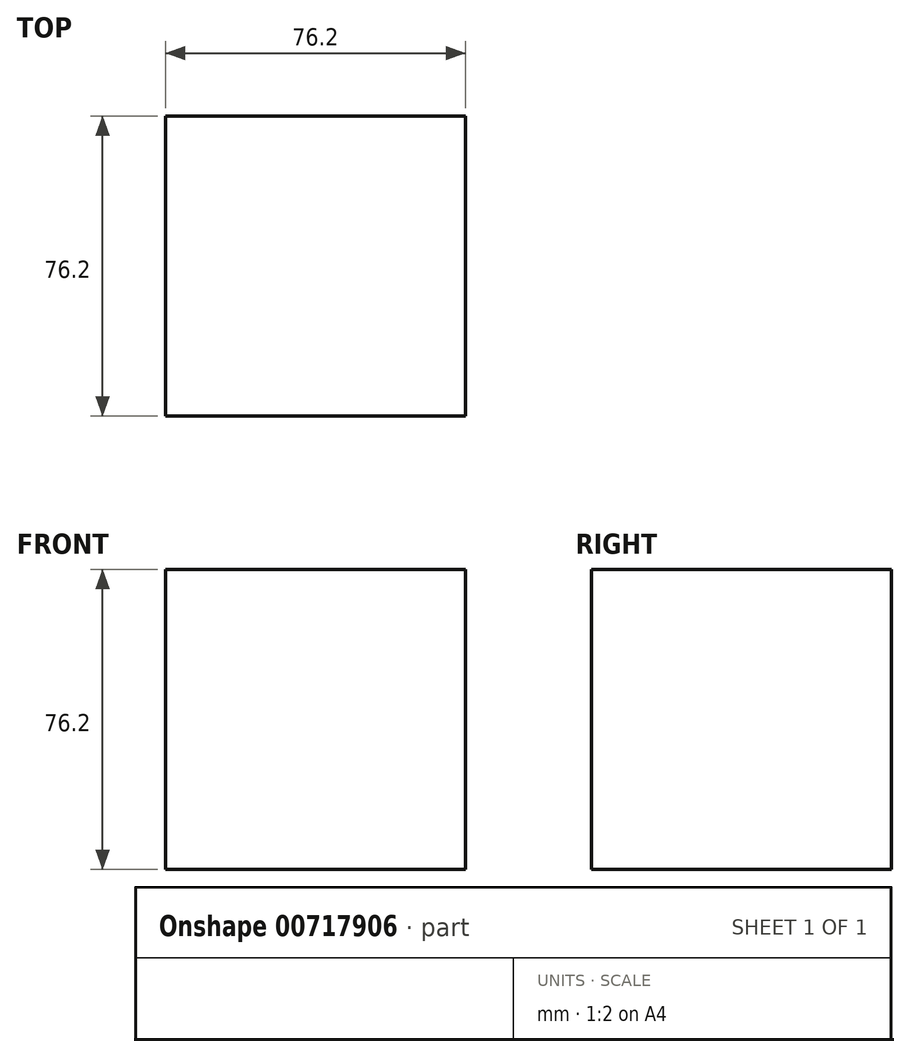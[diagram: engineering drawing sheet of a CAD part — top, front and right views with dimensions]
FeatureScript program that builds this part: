
annotation { "Feature Type Name" : "Feature", "Feature Type Description" : "" }
export const myFeature = defineFeature(function(context is Context, id is Id, definition is map)
    precondition{}
    {
        {
            var Q0;
            Q0=qCreatedBy(makeId("Front.planeOp"),FACE);
            var sketch = newSketch(context, id + "F0", { "sketchPlane" : qUnion([Q0])});
            skLineSegment(sketch, "E0.bottom", {"start": v(-40.3, 41.95) * mm, "end": v(35.9, 41.95) * mm});
            skLineSegment(sketch, "E0.top", {"start": v(-40.3, -34.25) * mm, "end": v(35.9, -34.25) * mm});
            skLineSegment(sketch, "E0.left", {"start": v(-40.3, 41.95) * mm, "end": v(-40.3, -34.25) * mm});
            skLineSegment(sketch, "E0.right", {"start": v(35.9, 41.95) * mm, "end": v(35.9, -34.25) * mm});
            skSolve(sketch);
        }
        {
            var Q0;
            Q0=makeQuery(id+"F0.imprint","IMPRINT",FACE,{"disambiguationData":[TD([[makeQuery(id+"F0.imprint","IMPRINT",EDGE,{"derivedFrom":sQuery(id+"F0.wireOp",EDGE,"E0.bottom")}),-1.0]])]});
            extrude(context, id + "F1", {"entities" : qUnion([Q0]), "depth" : 76.2 * mm, "offsetDistance" : 25.4 * mm});
        }
    });
